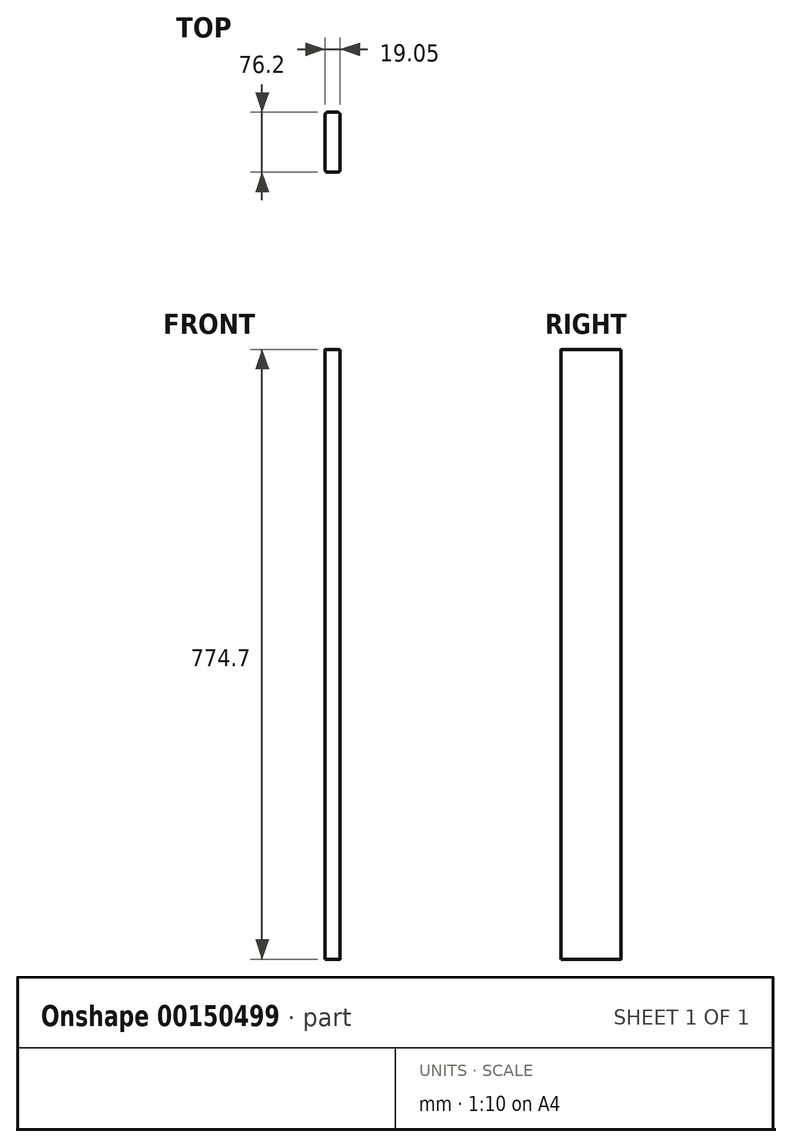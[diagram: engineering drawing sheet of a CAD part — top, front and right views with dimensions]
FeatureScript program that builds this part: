
annotation { "Feature Type Name" : "Feature", "Feature Type Description" : "" }
export const myFeature = defineFeature(function(context is Context, id is Id, definition is map)
    precondition{}
    {
        {
            var Q0;
            Q0=qCreatedBy(makeId("Right.planeOp"),FACE);
            var sketch = newSketch(context, id + "F0", { "sketchPlane" : qUnion([Q0])});
            skLineSegment(sketch, "E0.bottom", {"start": v(-40.45, 505.75) * mm, "end": v(35.75, 505.75) * mm});
            skLineSegment(sketch, "E0.top", {"start": v(-40.45, -268.95) * mm, "end": v(35.75, -268.95) * mm});
            skLineSegment(sketch, "E0.left", {"start": v(-40.45, 505.75) * mm, "end": v(-40.45, -268.95) * mm});
            skLineSegment(sketch, "E0.right", {"start": v(35.75, 505.75) * mm, "end": v(35.75, -268.95) * mm});
            skLineSegment(sketch, "E1", {"start": v(-2.35, 505.75) * mm, "end": v(-2.35, 467.65) * mm, "construction": true});
            skSolve(sketch);
        }
        {
            var Q0;
            Q0=makeQuery(id+"F0.imprint","IMPRINT",FACE,{"disambiguationData":[TD([[makeQuery(id+"F0.imprint","IMPRINT",EDGE,{"derivedFrom":sQuery(id+"F0.wireOp",EDGE,"E0.bottom")}),-1.0]])]});
            extrude(context, id + "F1", {"entities" : qUnion([Q0]), "depth" : 19.05 * mm});
        }
        {
            var Q0;
            Q0=makeQuery(id+"F1.opExtrude","CAP_EDGE",EDGE,{"disambiguationData":[OSD([sQuery(id+"F0.wireOp",EDGE,"E0.left")])],"isStart":true});
            var Q1;
            Q1=makeQuery(id+"F1.opExtrude","CAP_EDGE",EDGE,{"disambiguationData":[OSD([sQuery(id+"F0.wireOp",EDGE,"E0.left")])],"isStart":false});
            var Q2;
            Q2=makeQuery(id+"F1.opExtrude","CAP_EDGE",EDGE,{"disambiguationData":[OSD([sQuery(id+"F0.wireOp",EDGE,"E0.right")])],"isStart":true});
            var Q3;
            Q3=makeQuery(id+"F1.opExtrude","CAP_EDGE",EDGE,{"disambiguationData":[OSD([sQuery(id+"F0.wireOp",EDGE,"E0.right")])],"isStart":false});
            fillet(context, id + "F2", {"entities" : qUnion([Q0, Q1, Q2, Q3]), "radius" : 3.17 * mm, "tangentPropagation" : true, "allowEdgeOverflow" : false});
        }
    });
